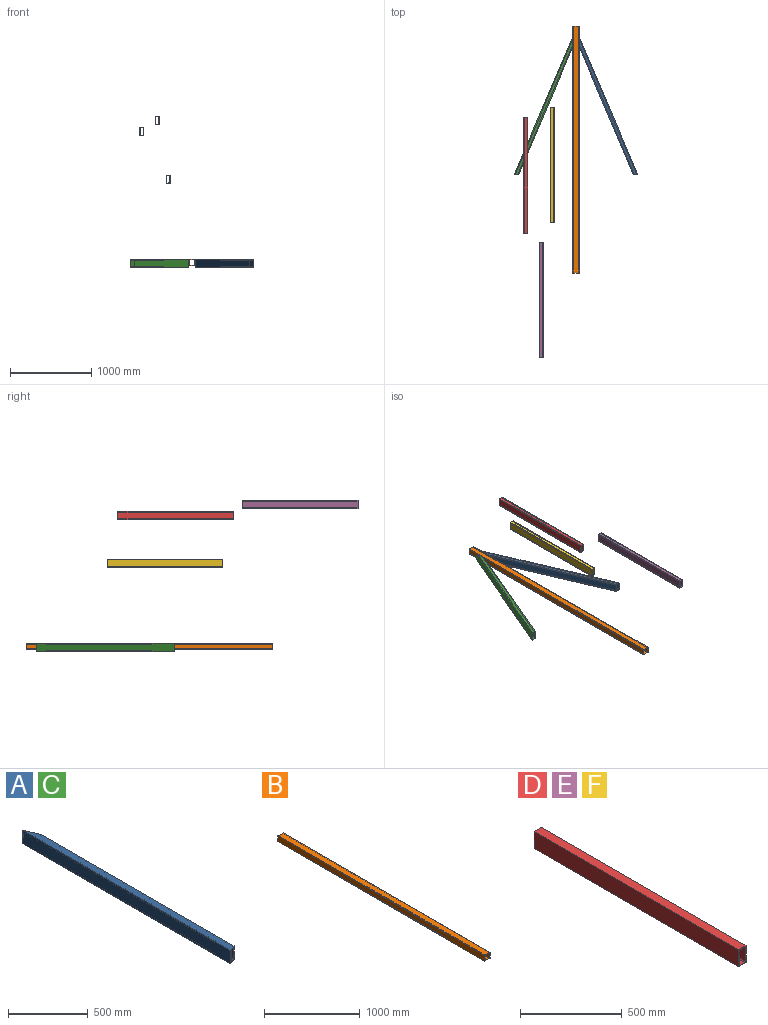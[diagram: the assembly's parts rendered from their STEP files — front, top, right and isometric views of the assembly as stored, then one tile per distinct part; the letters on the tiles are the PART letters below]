
ASSEMBLY  parts=6 mates=2
PART A: 14 faces, bbox 50.8x1849.4x101.6 mm
  f0: plane 1818.52x28.58mm, normal (0,0,-1), area 50830.6mm2, adj f1,f7,f8,f9
  f1: cylinder r=6.35mm len=1836.14mm, axis (0,1,0), area 18250.8mm2, adj f0,f2,f8,f9
  f2: plane 1836.14x79.38mm, normal (1,0,0), area 145743.9mm2, adj f1,f3,f8,f9
  f3: cylinder r=6.35mm len=1836.14mm, axis (0,1,0), area 18250.8mm2, adj f2,f4,f8,f9
  f4: plane 1818.52x28.58mm, normal (0,0,1), area 50830.6mm2, adj f3,f5,f8,f9
  f5: cylinder r=6.35mm len=1739.18mm, axis (0,1,0), area 17235.6mm2, adj f4,f6,f8,f9
  f6: plane 1721.55x79.38mm, normal (-1,0,0), area 136648.4mm2, adj f5,f7,f8,f9
  f7: cylinder r=6.35mm len=1739.18mm, axis (0,1,0), area 17235.6mm2, adj f0,f6,f8,f9
  f8: plane 101.6x50.8mm, normal (0.39,-0.92,0), area 1516.5mm2, adj f0,f1,f2,f3,f4,f5,f6,f7
  f9: plane 119.42x101.6mm, normal (0.92,0.39,0), area 3565.1mm2, adj f0,f1,f2,f3,f4,f5,f6,f7
  f10: plane 1849.37x50.8mm, normal (0,0,1), area 90365.5mm2, adj f8,f9,f12,f13
  f11: plane 1849.37x50.8mm, normal (0,0,-1), area 90365.5mm2, adj f8,f9,f12,f13
  f12: plane 1708.33x101.6mm, normal (1,0,0), area 173566.6mm2, adj f8,f9,f10,f11
  f13: plane 1849.37x101.6mm, normal (-1,0,0), area 187895.6mm2, adj f8,f9,f10,f11
PART B: 14 faces, bbox 76.2x3048x76.2 mm
  f0: plane 3048x76.2mm, normal (-1,0,0), area 232257.6mm2, adj f1,f11,f12,f13
  f1: plane 3048x76.2mm, normal (0,0,-1), area 232257.6mm2, adj f0,f2,f12,f13
  f2: plane 3048x76.2mm, normal (1,0,0), area 232257.6mm2, adj f1,f11,f12,f13
  f3: cylinder r=4.76mm len=3048mm, axis (0,1,0), area 22801.8mm2, adj f4,f10,f12,f13
  f4: plane 3048x57.15mm, normal (1,0,0), area 174193.2mm2, adj f3,f5,f12,f13
  f5: cylinder r=4.76mm len=3048mm, axis (0,1,0), area 22801.8mm2, adj f4,f6,f12,f13
  f6: plane 3048x57.15mm, normal (0,0,-1), area 174193.2mm2, adj f5,f7,f12,f13
  f7: cylinder r=4.76mm len=3048mm, axis (0,1,0), area 22801.8mm2, adj f6,f8,f12,f13
  f8: plane 3048x57.15mm, normal (-1,0,0), area 174193.2mm2, adj f7,f9,f12,f13
  f9: cylinder r=4.76mm len=3048mm, axis (0,1,0), area 22801.8mm2, adj f8,f10,f12,f13
  f10: plane 3048x57.15mm, normal (0,0,1), area 174193.2mm2, adj f3,f9,f12,f13
  f11: plane 3048x76.2mm, normal (0,0,1), area 232257.6mm2, adj f0,f2,f12,f13
  f12: plane 76.2x76.2mm, normal (0,-1,0), area 1380.4mm2, adj f0,f1,f2,f3,f4,f5,f6,f7
  f13: plane 76.2x76.2mm, normal (0,1,0), area 1380.4mm2, adj f0,f1,f2,f3,f4,f5,f6,f7
PART C: same geometry as A
PART D: 25 faces, bbox 50.8x1422.4x101.6 mm
  f0: plane 1422.4x101.6mm, normal (1,0,0), area 123617.3mm2, adj f3,f11,f12,f13,f14,f15,f16,f17
  f1: plane 1422.4x82.55mm, normal (-1,0,0), area 96520.6mm2, adj f6,f7,f12,f13,f14,f15,f16,f17
  f2: plane 1422.4x101.6mm, normal (-1,0,0), area 144515.8mm2, adj f3,f11,f12,f13
  f3: plane 1422.4x50.8mm, normal (0,0,-1), area 72257.9mm2, adj f0,f2,f12,f13
  f4: cylinder r=4.76mm len=1422.4mm, axis (0,1,0), area 10640.9mm2, adj f5,f10,f12,f13
  f5: plane 1422.4x31.75mm, normal (0,0,-1), area 45161.2mm2, adj f4,f6,f12,f13
  f6: cylinder r=4.76mm len=1422.4mm, axis (0,1,0), area 10640.9mm2, adj f1,f5,f12,f13
  f7: cylinder r=4.76mm len=1422.4mm, axis (0,1,0), area 10640.9mm2, adj f1,f8,f12,f13
  f8: plane 1422.4x31.75mm, normal (0,0,1), area 45161.2mm2, adj f7,f9,f12,f13
  f9: cylinder r=4.76mm len=1422.4mm, axis (0,1,0), area 10640.9mm2, adj f8,f10,f12,f13
  f10: plane 1422.4x82.55mm, normal (1,0,0), area 117419.1mm2, adj f4,f9,f12,f13
  f11: plane 1422.4x50.8mm, normal (0,0,1), area 72257.9mm2, adj f0,f2,f12,f13
  f12: plane 101.6x50.8mm, normal (0,-1,0), area 1380.4mm2, adj f0,f1,f2,f3,f4,f5,f6,f7
  f13: plane 101.6x50.8mm, normal (0,1,0), area 1380.4mm2, adj f0,f1,f2,f3,f4,f5,f6,f7
  f14: cylinder r=9.53mm len=19.05mm, axis (1,0,0), area 285mm2, adj f0,f1
  f15: cylinder r=9.53mm len=19.05mm, axis (1,0,0), area 285mm2, adj f0,f1
  f16: cylinder r=9.53mm len=19.05mm, axis (1,0,0), area 285mm2, adj f0,f1
  f17: plane 107.95x4.76mm, normal (0,0,-1), area 514.1mm2, adj f0,f1,f18,f20
  f18: cylinder r=31.75mm len=63.5mm, axis (1,0,0), area 475mm2, adj f0,f1,f17,f19
  f19: plane 107.95x4.76mm, normal (0,0,1), area 514.1mm2, adj f0,f1,f18,f20
  f20: cylinder r=31.75mm len=63.5mm, axis (1,0,0), area 475mm2, adj f0,f1,f17,f19
  f21: plane 107.95x4.76mm, normal (0,0,-1), area 514.1mm2, adj f0,f1,f22,f24
  f22: cylinder r=31.75mm len=63.5mm, axis (1,0,0), area 475mm2, adj f0,f1,f21,f23
  f23: plane 107.95x4.76mm, normal (0,0,1), area 514.1mm2, adj f0,f1,f22,f24
  f24: cylinder r=31.75mm len=63.5mm, axis (1,0,0), area 475mm2, adj f0,f1,f21,f23
PART E: same geometry as D
PART F: same geometry as D
PLACE A rot(axis=(0.2,-0.98,0),180deg) t=(0,-127,76.2)mm
PLACE B t=(-76.2,0,0)mm
PLACE C rot(axis=(0,0,-1),23deg) t=(-76.2,-127,-25.4)mm
PLACE D t=(-683.21,-1135.57,1603.86)mm
PLACE E t=(-492.94,-2676.35,1741.29)mm
PLACE F t=(-357.38,-1002.99,1016.48)mm
MATE fastened B.f2 <-> A.f9  axis (1,0,0) through (0,0,76.2)mm
MATE fastened B.f0 <-> C.f9  axis (-1,0,0) through (-76.2,0,76.2)mm
